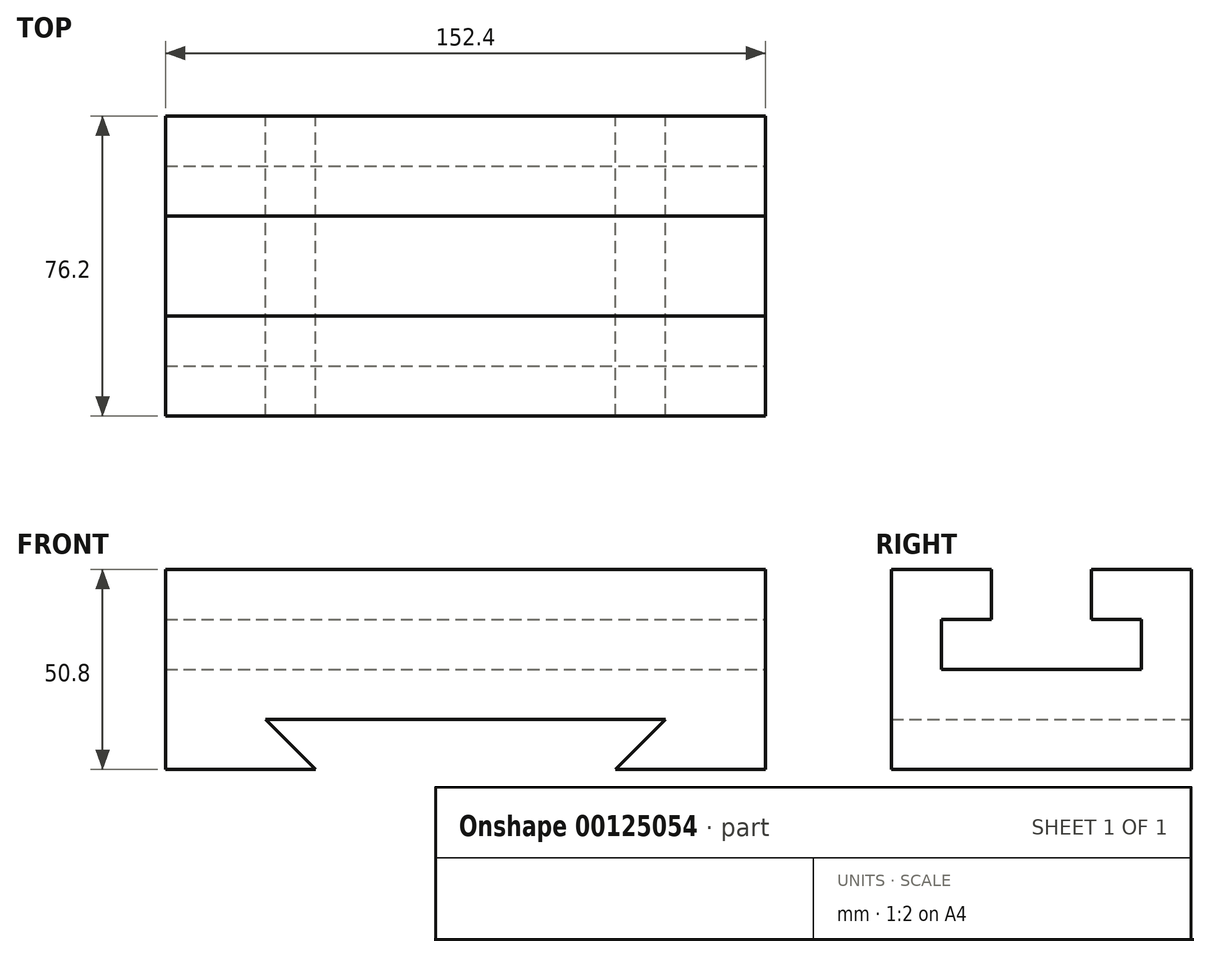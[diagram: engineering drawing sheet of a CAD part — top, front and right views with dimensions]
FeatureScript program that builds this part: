
annotation { "Feature Type Name" : "Feature", "Feature Type Description" : "" }
export const myFeature = defineFeature(function(context is Context, id is Id, definition is map)
    precondition{}
    {
        {
            var Q0;
            Q0=qCreatedBy(makeId("Front.planeOp"),FACE);
            var sketch = newSketch(context, id + "F0", { "sketchPlane" : qUnion([Q0])});
            skLineSegment(sketch, "E0.bottom", {"start": v(76.2, 25.4) * mm, "end": v(-76.2, 25.4) * mm});
            skLineSegment(sketch, "E0.left", {"start": v(76.2, 25.4) * mm, "end": v(76.2, -25.4) * mm});
            skLineSegment(sketch, "E0.right", {"start": v(-76.2, 25.4) * mm, "end": v(-76.2, -25.4) * mm});
            skPoint(sketch, "E0.middle", {"position": v(0, 0) * mm});
            skLineSegment(sketch, "E1", {"start": v(-76.2, -25.4) * mm, "end": v(-38.1, -25.4) * mm});
            skLineSegment(sketch, "E2", {"start": v(-50.8, -12.7) * mm, "end": v(-38.1, -25.4) * mm});
            skLineSegment(sketch, "E3", {"start": v(76.2, -25.4) * mm, "end": v(38.1, -25.4) * mm});
            skLineSegment(sketch, "E4", {"start": v(50.8, -12.7) * mm, "end": v(38.1, -25.4) * mm});
            skLineSegment(sketch, "E5", {"start": v(-50.8, -12.7) * mm, "end": v(50.8, -12.7) * mm});
            skSolve(sketch);
        }
        {
            var Q0;
            Q0 = qSketchRegion(id + "F0", true);
            extrude(context, id + "F1", {"entities" : qUnion([Q0]), "endBound" : BoundingType.SYMMETRIC, "depth" : 76.2 * mm});
        }
        {
            var Q0;
            Q0=makeQuery(id+"F1.opExtrude","SWEPT_FACE",FACE,{"disambiguationData":[OSD([sQuery(id+"F0.wireOp",EDGE,"E0.left")])]});
            var sketch = newSketch(context, id + "F2", { "sketchPlane" : qUnion([Q0])});
            skLineSegment(sketch, "E6", {"start": v(12.7, 25.4) * mm, "end": v(12.7, 12.7) * mm});
            skLineSegment(sketch, "E7", {"start": v(12.7, 12.7) * mm, "end": v(25.4, 12.7) * mm});
            skLineSegment(sketch, "E8", {"start": v(25.4, 12.7) * mm, "end": v(25.4, 0) * mm});
            skLineSegment(sketch, "E9", {"start": v(25.4, 0) * mm, "end": v(-25.4, 0) * mm});
            skLineSegment(sketch, "E10", {"start": v(-25.4, 0) * mm, "end": v(-25.4, 12.7) * mm});
            skLineSegment(sketch, "E11", {"start": v(-25.4, 12.7) * mm, "end": v(-12.7, 12.7) * mm});
            skLineSegment(sketch, "E12", {"start": v(-12.7, 12.7) * mm, "end": v(-12.7, 25.4) * mm});
            skLineSegment(sketch, "E13", {"start": v(-12.7, 25.4) * mm, "end": v(12.7, 25.4) * mm});
            skSolve(sketch);
        }
        {
            var Q0;
            Q0 = qSketchRegion(id + "F2", true);
            extrude(context, id + "F3", {"entities" : qUnion([Q0]), "operationType" : NewBodyOperationType.REMOVE, "endBound" : BoundingType.THROUGH_ALL, "oppositeDirection" : true, "depth" : 25.4 * mm});
        }
    });
